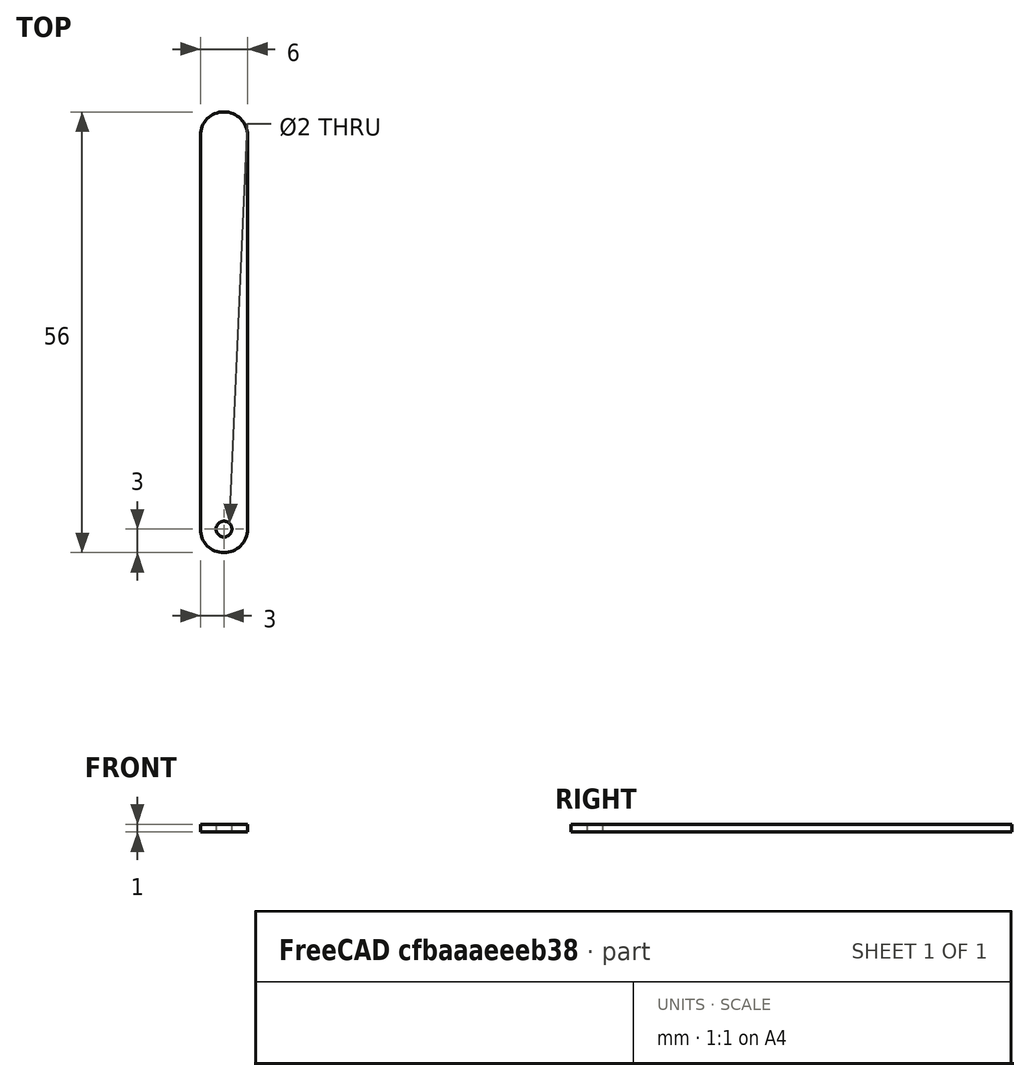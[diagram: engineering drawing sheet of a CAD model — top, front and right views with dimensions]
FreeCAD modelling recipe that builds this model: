
FCSTD DOCUMENT  (FreeCAD 0.19R24276 (Git))
Label: Stoika
License: All rights reserved
LicenseURL: http://en.wikipedia.org/wiki/All_rights_reserved
objects: Sketcher::SketchObject×1, PartDesign::Pad×1, PartDesign::Body×1
note: 4 computed .brp shape members not serialized (recipe doc carries the construction recipe); baked Part::Feature solids carry a one-line shape summary decoded from their .brp

FEATURE [Sketcher::SketchObject] Sketch
  FullyConstrained = true
  MapMode = 5
  Support = -> [XY_Plane]
  sketch-geometry (5):
    g0: ArcOfCircle CenterX=-9.0814e-12 CenterY=50 CenterZ=0 NormalX=0 NormalY=0 NormalZ=1 AngleXU=0 Radius=3 StartAngle=-1.612e-12 EndAngle=3.14159
    g1: ArcOfCircle CenterX=-3.9093e-12 CenterY=-1.4487e-12 CenterZ=0 NormalX=0 NormalY=0 NormalZ=1 AngleXU=0 Radius=3 StartAngle=3.14159 EndAngle=6.28319
    g2: LineSegment StartX=-3 StartY=50 StartZ=0 EndX=-3 EndY=8.1e-13 EndZ=0
    g3: LineSegment StartX=3 StartY=50 StartZ=0 EndX=3 EndY=-3.2827e-12 EndZ=0
    g4: Circle CenterX=-3.9093e-12 CenterY=-1.4487e-12 CenterZ=0 NormalX=0 NormalY=0 NormalZ=1 AngleXU=0 Radius=1
  constraints (11):
    c: Tangent(g0,g3) = 1.5708
    c: Tangent(g0,g2) = -1.5708
    c: Tangent(g2,g1) = -1.5708
    c: Tangent(g3,g1) = 1.5708
    c: Vertical(g2)
    c: Equal(g0,g1)
    c: DistanceY(g1,g0) = 50
    c: Coincident(g4,g1)
    c: Diameter(g4) = 2
    c: Radius(g1) = 3
    c: Coincident(g-1,g1)
FEATURE [PartDesign::Pad] Pad
  Direction = (1,1,1)
  Length = 1
  Length2 = 100
  Profile = -> Sketch
  Type = 0
FEATURE [PartDesign::Body] Body  label="Stoika"
  Group = -> [Sketch,Pad]
  Origin = -> Origin
  Tip = -> Pad
